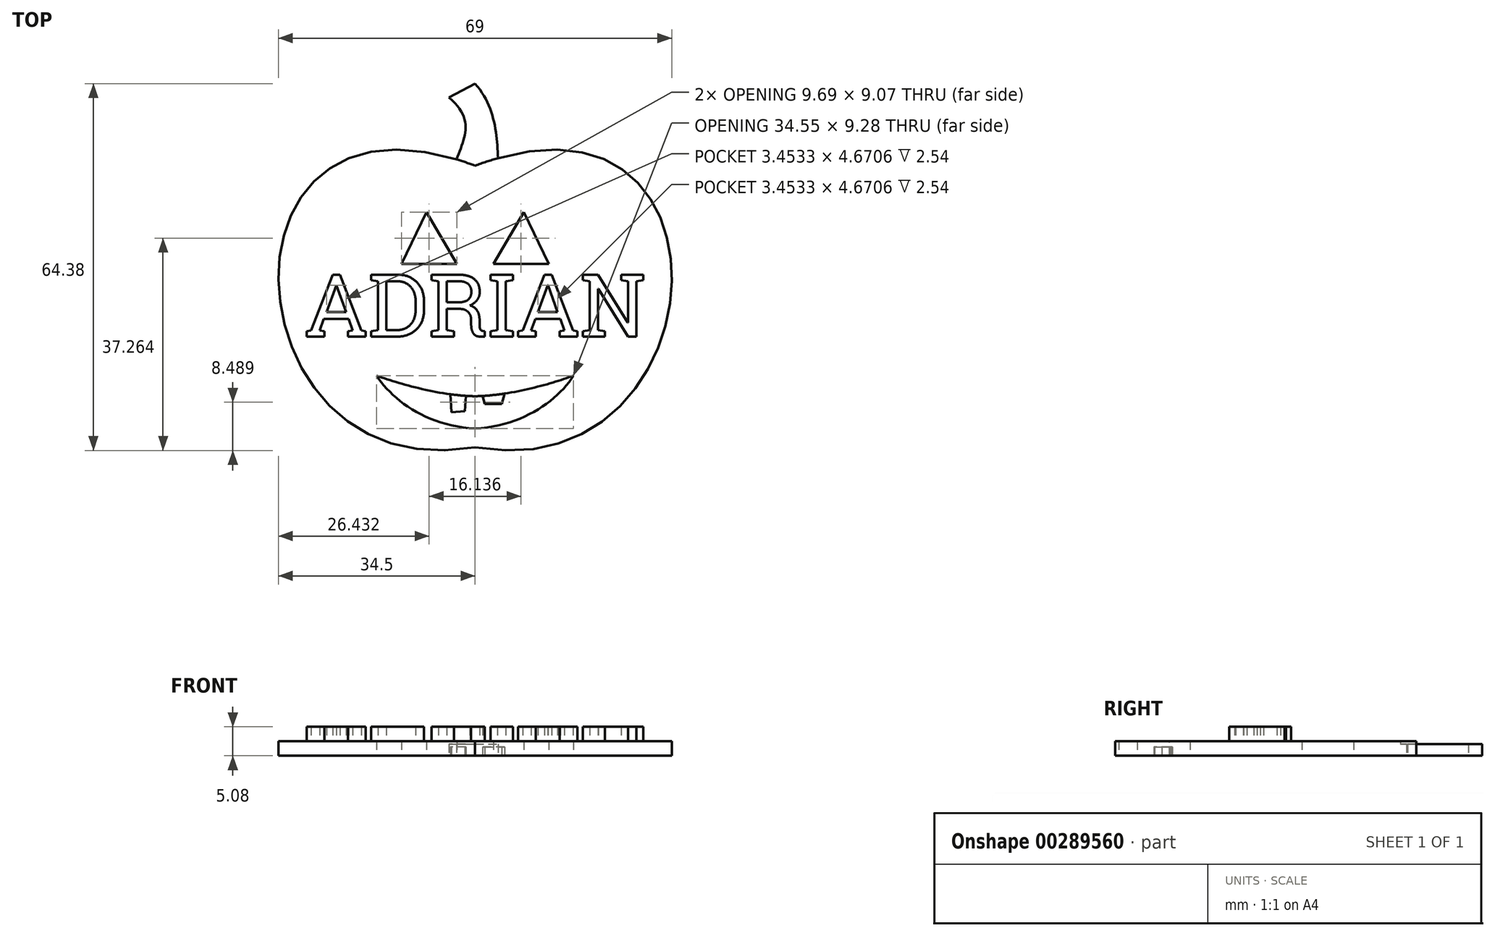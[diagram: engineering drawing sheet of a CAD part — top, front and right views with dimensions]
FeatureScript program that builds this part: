
annotation { "Feature Type Name" : "Feature", "Feature Type Description" : "" }
export const myFeature = defineFeature(function(context is Context, id is Id, definition is map)
    precondition{}
    {
        {
            var Q0;
            Q0=qCreatedBy(makeId("Top.planeOp"),FACE);
            var sketch = newSketch(context, id + "F0", { "sketchPlane" : qUnion([Q0])});
            skFitSpline(sketch, "E0", {"points": [v(0, 15.94) * mm, v(0, -33.47) * mm], "startDerivative": vector(-145.13, 54.29) * mm, "endDerivative": vector(130.7, 23.5) * mm});
            skFitSpline(sketch, "E1.MirrorCS", {"points": [v(0, 15.94) * mm, v(0, -33.47) * mm], "startDerivative": vector(145.13, 54.29) * mm, "endDerivative": vector(-130.7, 23.5) * mm});
            skPoint(sketch, "E2.startDerivative.orphan", {"position": v(-23.11, 0) * mm});
            skPoint(sketch, "E3.startDerivative.orphan", {"position": v(-8.75, 0) * mm});
            skFitSpline(sketch, "E4", {"points": [v(-3.24, 17.03) * mm, v(-4.57, 27.89) * mm], "startDerivative": vector(4.07, 11.5) * mm, "endDerivative": vector(-13.72, 11.58) * mm});
            skLineSegment(sketch, "E5", {"start": v(-4.57, 27.89) * mm, "end": v(0, 30.34) * mm});
            skFitSpline(sketch, "E6", {"points": [v(0, 30.34) * mm, v(4.01, 17.26) * mm], "startDerivative": vector(10.5, -11.93) * mm, "endDerivative": vector(0.53, -12.68) * mm});
            skLineSegment(sketch, "E7", {"start": v(-12.91, -1.3) * mm, "end": v(-3.22, -1.3) * mm});
            skLineSegment(sketch, "E8", {"start": v(-3.22, -1.3) * mm, "end": v(-8.54, 7.76) * mm});
            skLineSegment(sketch, "E9", {"start": v(-8.54, 7.76) * mm, "end": v(-12.91, -1.3) * mm});
            skFitSpline(sketch, "E10", {"points": [v(0, -30.2) * mm, v(-17.27, -20.9) * mm], "startDerivative": vector(-24.99, 1.25) * mm, "endDerivative": vector(-8.44, 13.13) * mm});
            skFitSpline(sketch, "E11", {"points": [v(-17.27, -20.9) * mm, v(0, -24.52) * mm], "startDerivative": vector(12.63, -4.59) * mm, "endDerivative": vector(18.38, -0.34) * mm});
            skLineSegment(sketch, "E12.MirrorCS", {"start": v(3.22, -1.3) * mm, "end": v(8.54, 7.76) * mm});
            skLineSegment(sketch, "E13.MirrorCS", {"start": v(8.54, 7.76) * mm, "end": v(12.91, -1.3) * mm});
            skLineSegment(sketch, "E14.MirrorCS", {"start": v(12.91, -1.3) * mm, "end": v(3.22, -1.3) * mm});
            skFitSpline(sketch, "E15.MirrorCS", {"points": [v(17.27, -20.9) * mm, v(0, -24.52) * mm], "startDerivative": vector(-12.63, -4.59) * mm, "endDerivative": vector(-18.38, -0.34) * mm});
            skFitSpline(sketch, "E16.MirrorCS", {"points": [v(0, -30.2) * mm, v(17.27, -20.9) * mm], "startDerivative": vector(24.99, 1.25) * mm, "endDerivative": vector(8.44, 13.13) * mm});
            skLineSegment(sketch, "E17", {"start": v(1.33, -24.47) * mm, "end": v(1.68, -25.88) * mm});
            skLineSegment(sketch, "E18", {"start": v(1.68, -25.88) * mm, "end": v(4.68, -25.88) * mm});
            skLineSegment(sketch, "E19", {"start": v(4.68, -25.88) * mm, "end": v(5.16, -24.06) * mm});
            skLineSegment(sketch, "E20", {"start": v(-1.62, -24.45) * mm, "end": v(-1.83, -27.16) * mm});
            skLineSegment(sketch, "E21", {"start": v(-1.83, -27.16) * mm, "end": v(-4.13, -27.3) * mm});
            skLineSegment(sketch, "E22", {"start": v(-4.13, -27.3) * mm, "end": v(-4.33, -24.18) * mm});
            skText(sketch, "E23", { "text": "ADRIAN", "fontName": "RobotoSlab-Regular.ttf"});
            const initialGuessF0  = {"E23": [-0.02999, -0.01406, 1, 0, 0.01102]};
            skSetInitialGuess(sketch, initialGuessF0);
            skSolve(sketch);
        }
        {
            var Q0;
            Q0=makeQuery(id+"F0.imprint","IMPRINT",FACE,{"disambiguationData":[TD([[makeQuery(id+"F0.imprint","IMPRINT",EDGE,{"derivedFrom":sQuery(id+"F0.wireOp",EDGE,"0ed1a2ba-a753-4832-a2ec-c21e0d6adfd2.sketch_text.stroke-64")}),1.0]])]});
            var Q1;
            Q1=makeQuery(id+"F0.imprint","IMPRINT",FACE,{"disambiguationData":[TD([[makeQuery(id+"F0.imprint","IMPRINT",EDGE,{"derivedFrom":sQuery(id+"F0.wireOp",EDGE,"0ed1a2ba-a753-4832-a2ec-c21e0d6adfd2.sketch_text.stroke-33")}),1.0]])]});
            var Q2;
            Q2=makeQuery(id+"F0.imprint","IMPRINT",FACE,{"disambiguationData":[TD([[makeQuery(id+"F0.imprint","IMPRINT",EDGE,{"derivedFrom":sQuery(id+"F0.wireOp",EDGE,"ee870e3c-5ad4-4695-90e3-c3f5bd1c7ecf.sketch_text.stroke-34")}),1.0]])]});
            var Q3;
            Q3=makeQuery(id+"F0.imprint","IMPRINT",FACE,{"disambiguationData":[TD([[makeQuery(id+"F0.imprint","IMPRINT",EDGE,{"derivedFrom":sQuery(id+"F0.wireOp",EDGE,"ee870e3c-5ad4-4695-90e3-c3f5bd1c7ecf.sketch_text.stroke-139")}),1.0]])]});
            var Q4;
            Q4=makeQuery(id+"F0.imprint","IMPRINT",FACE,{"disambiguationData":[TD([[makeQuery(id+"F0.imprint","IMPRINT",EDGE,{"derivedFrom":sQuery(id+"F0.wireOp",EDGE,"7820292b-a5dd-43b0-a134-8cac0a058638.sketch_text.stroke-34")}),1.0]])]});
            var Q5;
            Q5=makeQuery(id+"F0.imprint","IMPRINT",FACE,{"disambiguationData":[TD([[makeQuery(id+"F0.imprint","IMPRINT",EDGE,{"derivedFrom":sQuery(id+"F0.wireOp",EDGE,"7820292b-a5dd-43b0-a134-8cac0a058638.sketch_text.stroke-72")}),1.0]])]});
            var Q6;
            Q6=makeQuery(id+"F0.imprint","IMPRINT",FACE,{"disambiguationData":[TD([[makeQuery(id+"F0.imprint","IMPRINT",EDGE,{"derivedFrom":sQuery(id+"F0.wireOp",EDGE,"7820292b-a5dd-43b0-a134-8cac0a058638.sketch_text.stroke-105")}),1.0]])]});
            var Q7;
            Q7=makeQuery(id+"F0.imprint","IMPRINT",FACE,{"disambiguationData":[TD([[makeQuery(id+"F0.imprint","IMPRINT",EDGE,{"derivedFrom":sQuery(id+"F0.wireOp",EDGE,"7820292b-a5dd-43b0-a134-8cac0a058638.sketch_text.stroke-98")}),1.0]])]});
            var Q8;
            Q8=makeQuery(id+"F0.imprint","IMPRINT",FACE,{"disambiguationData":[TD([[makeQuery(id+"F0.imprint","IMPRINT",EDGE,{"derivedFrom":sQuery(id+"F0.wireOp",EDGE,"e767cda8-1620-4fd0-b680-d23c8d51958f.sketch_text.stroke-42")}),1.0]])]});
            var Q9;
            Q9=makeQuery(id+"F0.imprint","IMPRINT",FACE,{"disambiguationData":[TD([[makeQuery(id+"F0.imprint","IMPRINT",EDGE,{"derivedFrom":sQuery(id+"F0.wireOp",EDGE,"8da3b25e-50d5-4822-ab9c-2fc53cc63223.sketch_text.stroke-26")}),1.0]])]});
            var Q10;
            Q10=makeQuery(id+"F0.imprint","IMPRINT",FACE,{"disambiguationData":[TD([[makeQuery(id+"F0.imprint","IMPRINT",EDGE,{"derivedFrom":sQuery(id+"F0.wireOp",EDGE,"8da3b25e-50d5-4822-ab9c-2fc53cc63223.sketch_text.stroke-8")}),1.0]])]});
            var Q11;
            Q11=makeQuery(id+"F0.imprint","IMPRINT",FACE,{"disambiguationData":[TD([[makeQuery(id+"F0.imprint","IMPRINT",EDGE,{"derivedFrom":sQuery(id+"F0.wireOp",EDGE,"8cdec8b8-4fa5-4737-ac4f-f9a898c16520.sketch_text.stroke-34")}),1.0]])]});
            var Q12;
            Q12=makeQuery(id+"F0.imprint","IMPRINT",FACE,{"disambiguationData":[TD([[makeQuery(id+"F0.imprint","IMPRINT",EDGE,{"derivedFrom":sQuery(id+"F0.wireOp",EDGE,"8cdec8b8-4fa5-4737-ac4f-f9a898c16520.sketch_text.stroke-83")}),1.0]])]});
            var Q13;
            Q13=makeQuery(id+"F0.imprint","IMPRINT",FACE,{"disambiguationData":[TD([[makeQuery(id+"F0.imprint","IMPRINT",EDGE,{"derivedFrom":sQuery(id+"F0.wireOp",EDGE,"E7")}),-1.0]])]});
            var Q14;
            Q14=makeQuery(id+"F0.imprint","IMPRINT",FACE,{"disambiguationData":[TD([[makeQuery(id+"F0.imprint","IMPRINT",EDGE,{"derivedFrom":sQuery(id+"F0.wireOp",EDGE,"c25d6d70-2b21-4074-971c-57c7a2cbd43c.sketch_text.stroke-34")}),1.0]])]});
            var Q15;
            Q15=makeQuery(id+"F0.imprint","IMPRINT",FACE,{"disambiguationData":[TD([[makeQuery(id+"F0.imprint","IMPRINT",EDGE,{"derivedFrom":sQuery(id+"F0.wireOp",EDGE,"c25d6d70-2b21-4074-971c-57c7a2cbd43c.sketch_text.stroke-83")}),1.0]])]});
            var Q16;
            Q16=makeQuery(id+"F0.imprint","IMPRINT",FACE,{"disambiguationData":[TD([[makeQuery(id+"F0.imprint","IMPRINT",EDGE,{"derivedFrom":sQuery(id+"F0.wireOp",EDGE,"c25d6d70-2b21-4074-971c-57c7a2cbd43c.sketch_text.stroke-140")}),1.0]])]});
            extrude(context, id + "F1", {"entities" : qUnion([Q0, Q1, Q2, Q3, Q4, Q5, Q6, Q7, Q8, Q9, Q10, Q11, Q12, Q13, Q14, Q15, Q16]), "depth" : 2.54 * mm});
        }
        {
            var Q0;
            {var subQ0=sQuery(id+"F0.wireOp",EDGE,"E20");Q0=makeQuery(id+"F0.imprint","IMPRINT",FACE,{"disambiguationData":[TD([[makeQuery(id+"F0.imprint","IMPRINT",EDGE,{"derivedFrom":subQ0}),-1.0]])]});}
            var Q1;
            {var subQ0=sQuery(id+"F0.wireOp",EDGE,"E17");Q1=makeQuery(id+"F0.imprint","IMPRINT",FACE,{"disambiguationData":[TD([[makeQuery(id+"F0.imprint","IMPRINT",EDGE,{"derivedFrom":subQ0}),1.0]])]});}
            extrude(context, id + "F2", {"entities" : qUnion([Q0, Q1]), "operationType" : NewBodyOperationType.ADD, "depth" : 1.52 * mm});
        }
        {
            var Q0;
            {var subQ0=sQuery(id+"F0.wireOp",EDGE,"E4");Q0=makeQuery(id+"F0.imprint","IMPRINT",FACE,{"disambiguationData":[TD([[makeQuery(id+"F0.imprint","IMPRINT",EDGE,{"derivedFrom":subQ0}),-1.0]])]});}
            extrude(context, id + "F3", {"entities" : qUnion([Q0]), "operationType" : NewBodyOperationType.ADD, "depth" : 2.03 * mm});
        }
        {
            var Q0;
            Q0=makeQuery(id+"F0.imprint","IMPRINT",FACE,{"disambiguationData":[TD([[makeQuery(id+"F0.imprint","IMPRINT",EDGE,{"derivedFrom":sQuery(id+"F0.wireOp",EDGE,"E23.sketch_text.stroke-0")}),-1.0]])]});
            var Q1;
            Q1=makeQuery(id+"F0.imprint","IMPRINT",FACE,{"disambiguationData":[TD([[makeQuery(id+"F0.imprint","IMPRINT",EDGE,{"derivedFrom":sQuery(id+"F0.wireOp",EDGE,"E23.sketch_text.stroke-20")}),-1.0]])]});
            var Q2;
            Q2=makeQuery(id+"F0.imprint","IMPRINT",FACE,{"disambiguationData":[TD([[makeQuery(id+"F0.imprint","IMPRINT",EDGE,{"derivedFrom":sQuery(id+"F0.wireOp",EDGE,"E23.sketch_text.stroke-41")}),-1.0]])]});
            var Q3;
            Q3=makeQuery(id+"F0.imprint","IMPRINT",FACE,{"disambiguationData":[TD([[makeQuery(id+"F0.imprint","IMPRINT",EDGE,{"derivedFrom":sQuery(id+"F0.wireOp",EDGE,"E23.sketch_text.stroke-77")}),-1.0]])]});
            var Q4;
            Q4=makeQuery(id+"F0.imprint","IMPRINT",FACE,{"disambiguationData":[TD([[makeQuery(id+"F0.imprint","IMPRINT",EDGE,{"derivedFrom":sQuery(id+"F0.wireOp",EDGE,"E23.sketch_text.stroke-89")}),-1.0]])]});
            var Q5;
            Q5=makeQuery(id+"F0.imprint","IMPRINT",FACE,{"disambiguationData":[TD([[makeQuery(id+"F0.imprint","IMPRINT",EDGE,{"derivedFrom":sQuery(id+"F0.wireOp",EDGE,"E23.sketch_text.stroke-109")}),-1.0]])]});
            extrude(context, id + "F4", {"entities" : qUnion([Q0, Q1, Q2, Q3, Q4, Q5]), "operationType" : NewBodyOperationType.ADD, "depth" : 5.08 * mm});
        }
        {
            var Q0;
            Q0=makeQuery(id+"F0.imprint","IMPRINT",FACE,{"disambiguationData":[TD([[makeQuery(id+"F0.imprint","IMPRINT",EDGE,{"derivedFrom":sQuery(id+"F0.wireOp",EDGE,"4cf0f898-6d5f-45e3-9245-bb80a5881bd1.sketch_text.stroke-11")}),1.0]])]});
            var Q1;
            Q1=makeQuery(id+"F0.imprint","IMPRINT",FACE,{"disambiguationData":[TD([[makeQuery(id+"F0.imprint","IMPRINT",EDGE,{"derivedFrom":sQuery(id+"F0.wireOp",EDGE,"4cf0f898-6d5f-45e3-9245-bb80a5881bd1.sketch_text.stroke-26")}),1.0]])]});
            var Q2;
            Q2=makeQuery(id+"F0.imprint","IMPRINT",FACE,{"disambiguationData":[TD([[makeQuery(id+"F0.imprint","IMPRINT",EDGE,{"derivedFrom":sQuery(id+"F0.wireOp",EDGE,"4cf0f898-6d5f-45e3-9245-bb80a5881bd1.sketch_text.stroke-66")}),1.0]])]});
            var Q3;
            Q3=makeQuery(id+"F0.imprint","IMPRINT",FACE,{"disambiguationData":[TD([[makeQuery(id+"F0.imprint","IMPRINT",EDGE,{"derivedFrom":sQuery(id+"F0.wireOp",EDGE,"4cf0f898-6d5f-45e3-9245-bb80a5881bd1.sketch_text.stroke-96")}),1.0]])]});
            var Q4;
            Q4=makeQuery(id+"F0.imprint","IMPRINT",FACE,{"disambiguationData":[TD([[makeQuery(id+"F0.imprint","IMPRINT",EDGE,{"derivedFrom":sQuery(id+"F0.wireOp",EDGE,"a1e223c0-dca9-4135-b865-388a2cdc4b31.sketch_text.stroke-26")}),1.0]])]});
            var Q5;
            Q5=makeQuery(id+"F0.imprint","IMPRINT",FACE,{"disambiguationData":[TD([[makeQuery(id+"F0.imprint","IMPRINT",EDGE,{"derivedFrom":sQuery(id+"F0.wireOp",EDGE,"a1e223c0-dca9-4135-b865-388a2cdc4b31.sketch_text.stroke-42")}),1.0]])]});
            var Q6;
            Q6=makeQuery(id+"F0.imprint","IMPRINT",FACE,{"disambiguationData":[TD([[makeQuery(id+"F0.imprint","IMPRINT",EDGE,{"derivedFrom":sQuery(id+"F0.wireOp",EDGE,"a1e223c0-dca9-4135-b865-388a2cdc4b31.sketch_text.stroke-66")}),1.0]])]});
            var Q7;
            Q7=makeQuery(id+"F0.imprint","IMPRINT",FACE,{"disambiguationData":[TD([[makeQuery(id+"F0.imprint","IMPRINT",EDGE,{"derivedFrom":sQuery(id+"F0.wireOp",EDGE,"fbf27dbf-355d-4cea-9264-9a6780ff7270.sketch_text.stroke-16")}),1.0]])]});
            var Q8;
            Q8=makeQuery(id+"F0.imprint","IMPRINT",FACE,{"disambiguationData":[TD([[makeQuery(id+"F0.imprint","IMPRINT",EDGE,{"derivedFrom":sQuery(id+"F0.wireOp",EDGE,"fbf27dbf-355d-4cea-9264-9a6780ff7270.sketch_text.stroke-49")}),1.0]])]});
            var Q9;
            Q9=makeQuery(id+"F0.imprint","IMPRINT",FACE,{"disambiguationData":[TD([[makeQuery(id+"F0.imprint","IMPRINT",EDGE,{"derivedFrom":sQuery(id+"F0.wireOp",EDGE,"fbf27dbf-355d-4cea-9264-9a6780ff7270.sketch_text.stroke-84")}),1.0]])]});
            var Q10;
            Q10=makeQuery(id+"F0.imprint","IMPRINT",FACE,{"disambiguationData":[TD([[makeQuery(id+"F0.imprint","IMPRINT",EDGE,{"derivedFrom":sQuery(id+"F0.wireOp",EDGE,"447417c4-80c4-44ae-b588-759ab7125f7e.sketch_text.stroke-119")}),1.0]])]});
            var Q11;
            Q11=makeQuery(id+"F0.imprint","IMPRINT",FACE,{"disambiguationData":[TD([[makeQuery(id+"F0.imprint","IMPRINT",EDGE,{"derivedFrom":sQuery(id+"F0.wireOp",EDGE,"447417c4-80c4-44ae-b588-759ab7125f7e.sketch_text.stroke-90")}),1.0]])]});
            var Q12;
            Q12=makeQuery(id+"F0.imprint","IMPRINT",FACE,{"disambiguationData":[TD([[makeQuery(id+"F0.imprint","IMPRINT",EDGE,{"derivedFrom":sQuery(id+"F0.wireOp",EDGE,"447417c4-80c4-44ae-b588-759ab7125f7e.sketch_text.stroke-57")}),1.0]])]});
            var Q13;
            Q13=makeQuery(id+"F0.imprint","IMPRINT",FACE,{"disambiguationData":[TD([[makeQuery(id+"F0.imprint","IMPRINT",EDGE,{"derivedFrom":sQuery(id+"F0.wireOp",EDGE,"026360f7-0841-49fe-a43f-05eb81eb0128.sketch_text.stroke-32")}),1.0]])]});
            var Q14;
            Q14=makeQuery(id+"F0.imprint","IMPRINT",FACE,{"disambiguationData":[TD([[makeQuery(id+"F0.imprint","IMPRINT",EDGE,{"derivedFrom":sQuery(id+"F0.wireOp",EDGE,"026360f7-0841-49fe-a43f-05eb81eb0128.sketch_text.stroke-73")}),1.0]])]});
            var Q15;
            Q15=makeQuery(id+"F0.imprint","IMPRINT",FACE,{"disambiguationData":[TD([[makeQuery(id+"F0.imprint","IMPRINT",EDGE,{"derivedFrom":sQuery(id+"F0.wireOp",EDGE,"026360f7-0841-49fe-a43f-05eb81eb0128.sketch_text.stroke-91")}),1.0]])]});
            var Q16;
            Q16=makeQuery(id+"F0.imprint","IMPRINT",FACE,{"disambiguationData":[TD([[makeQuery(id+"F0.imprint","IMPRINT",EDGE,{"derivedFrom":sQuery(id+"F0.wireOp",EDGE,"2e2df881-9918-426d-9d6f-0d18e951021d.sketch_text.stroke-34")}),1.0]])]});
            var Q17;
            Q17=makeQuery(id+"F0.imprint","IMPRINT",FACE,{"disambiguationData":[TD([[makeQuery(id+"F0.imprint","IMPRINT",EDGE,{"derivedFrom":sQuery(id+"F0.wireOp",EDGE,"259812ea-c8a9-4945-9dcf-6c6f8a6260b1.sketch_text.stroke-102")}),1.0]])]});
            var Q18;
            Q18=makeQuery(id+"F0.imprint","IMPRINT",FACE,{"disambiguationData":[TD([[makeQuery(id+"F0.imprint","IMPRINT",EDGE,{"derivedFrom":sQuery(id+"F0.wireOp",EDGE,"5c877be5-1c7e-421c-ad2e-2bb15e631ec6.sketch_text.stroke-74")}),1.0]])]});
            var Q19;
            Q19=makeQuery(id+"F0.imprint","IMPRINT",FACE,{"disambiguationData":[TD([[makeQuery(id+"F0.imprint","IMPRINT",EDGE,{"derivedFrom":sQuery(id+"F0.wireOp",EDGE,"5c877be5-1c7e-421c-ad2e-2bb15e631ec6.sketch_text.stroke-98")}),1.0]])]});
            var Q20;
            Q20=makeQuery(id+"F0.imprint","IMPRINT",FACE,{"disambiguationData":[TD([[makeQuery(id+"F0.imprint","IMPRINT",EDGE,{"derivedFrom":sQuery(id+"F0.wireOp",EDGE,"E23.sketch_text.stroke-33")}),1.0]])]});
            var Q21;
            Q21=makeQuery(id+"F0.imprint","IMPRINT",FACE,{"disambiguationData":[TD([[makeQuery(id+"F0.imprint","IMPRINT",EDGE,{"derivedFrom":sQuery(id+"F0.wireOp",EDGE,"E23.sketch_text.stroke-70")}),1.0]])]});
            var Q22;
            Q22=makeQuery(id+"F0.imprint","IMPRINT",FACE,{"disambiguationData":[TD([[makeQuery(id+"F0.imprint","IMPRINT",EDGE,{"derivedFrom":sQuery(id+"F0.wireOp",EDGE,"E23.sketch_text.stroke-105")}),1.0]])]});
            var Q23;
            Q23=makeQuery(id+"F0.imprint","IMPRINT",FACE,{"disambiguationData":[TD([[makeQuery(id+"F0.imprint","IMPRINT",EDGE,{"derivedFrom":sQuery(id+"F0.wireOp",EDGE,"E23.sketch_text.stroke-16")}),1.0]])]});
            extrude(context, id + "F5", {"entities" : qUnion([Q0, Q1, Q2, Q3, Q4, Q5, Q6, Q7, Q8, Q9, Q10, Q11, Q12, Q13, Q14, Q15, Q16, Q17, Q18, Q19, Q20, Q21, Q22, Q23]), "operationType" : NewBodyOperationType.ADD, "depth" : 2.54 * mm});
        }
    });
